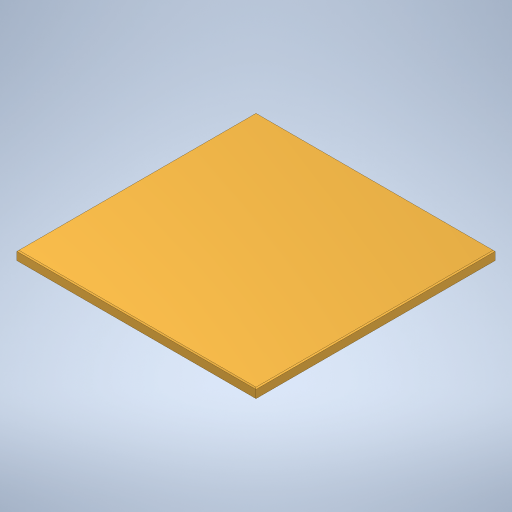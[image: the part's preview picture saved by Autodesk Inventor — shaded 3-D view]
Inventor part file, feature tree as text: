
AUTODESK INVENTOR PART (.ipt)
format: ipt  version: 2023 (Build 270158000, 158)  size: 231,424 bytes
history: native  units: mm
features: other x1, extrude x1, chamfer x1, sketch x1
ambient origin geometry x8: Origin, YZ Plane, XZ Plane, XY Plane, X Axis, Y Axis, Z Axis, Center Point
bodies: Body1 (feature_tree)
feature tree (4):
  other  "Sólido1"
  extrude  "Extrusão1"  Depth=120.0mm
  chamfer  "Chamfer1"  Distance=5.0mm
  sketch  "Esboço1"  dims[d0=120.0mm d1=120.0mm d2=5.0mm d3=0.0mm d4=0.5mm d5=2.0mm d6=45.0deg]
